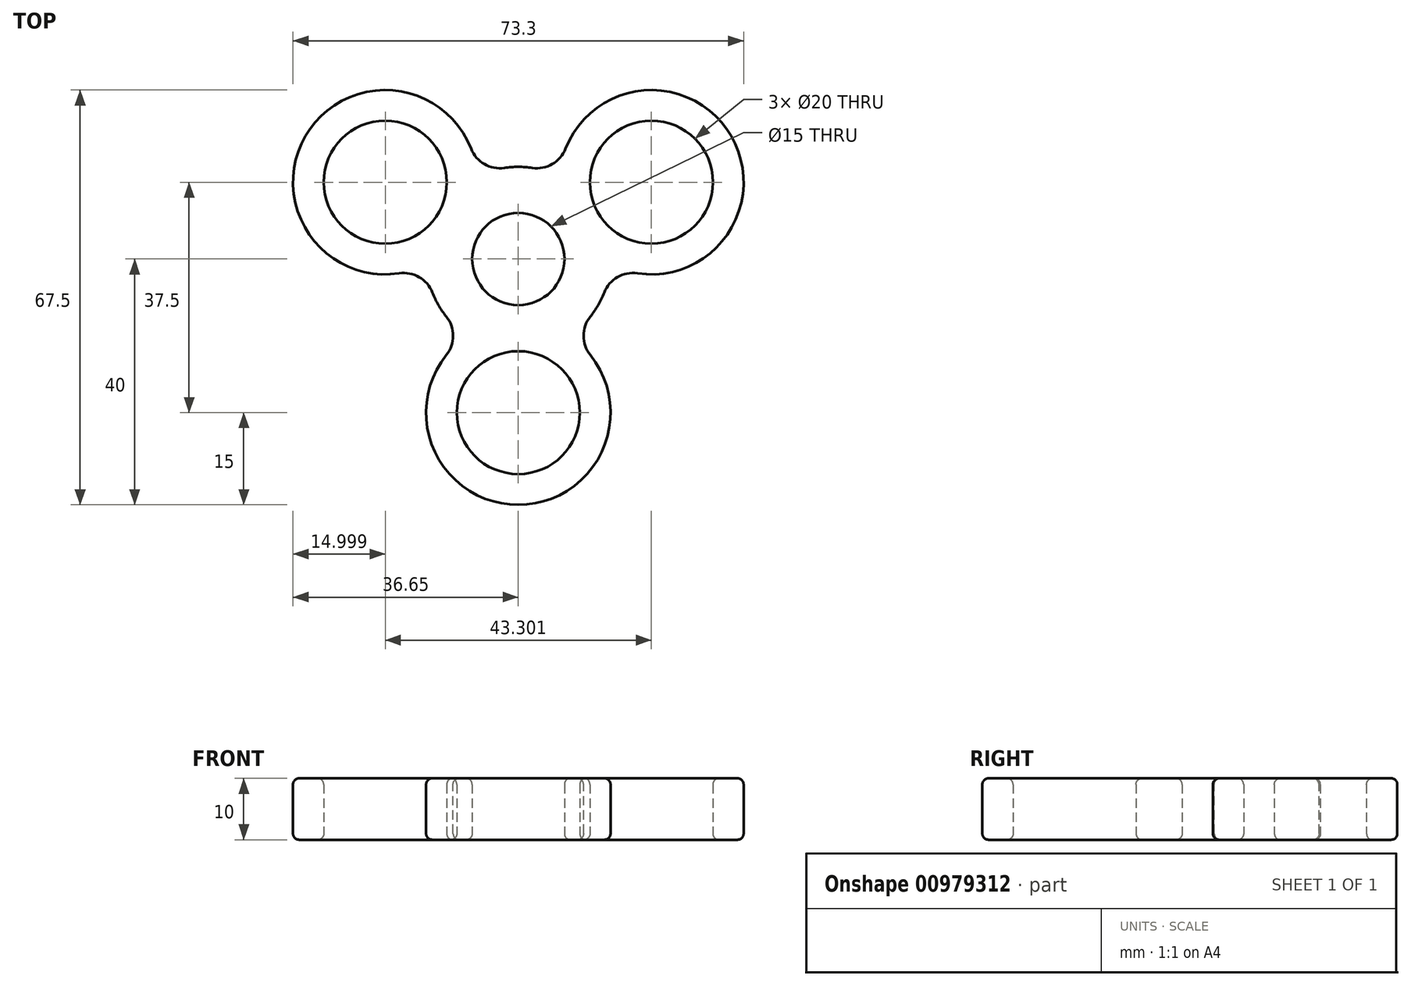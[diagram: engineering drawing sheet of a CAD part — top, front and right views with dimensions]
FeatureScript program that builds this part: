
annotation { "Feature Type Name" : "Feature", "Feature Type Description" : "" }
export const myFeature = defineFeature(function(context is Context, id is Id, definition is map)
    precondition{}
    {
        {
            var Q0;
            Q0=qCreatedBy(makeId("Top.planeOp"),FACE);
            var sketch = newSketch(context, id + "F0", { "sketchPlane" : qUnion([Q0])});
            skCircle(sketch, "E0", {"center": v(0, 0) * mm, "radius": 7.5 * mm});
            skCircle(sketch, "E1", {"center": v(0, 0) * mm, "radius": 15 * mm});
            skLineSegment(sketch, "E2", {"start": v(0, 0) * mm, "end": v(0, -25) * mm, "construction": true});
            skCircle(sketch, "E3", {"center": v(0, -25) * mm, "radius": 15 * mm});
            skCircle(sketch, "E4", {"center": v(0, -25) * mm, "radius": 10 * mm});
            skCircle(sketch, "E5.1.0", {"center": v(21.65, 12.5) * mm, "radius": 15 * mm});
            skCircle(sketch, "E5.1.1", {"center": v(21.65, 12.5) * mm, "radius": 10 * mm});
            skCircle(sketch, "E5.2.0", {"center": v(-21.65, 12.5) * mm, "radius": 15 * mm});
            skCircle(sketch, "E5.2.1", {"center": v(-21.65, 12.5) * mm, "radius": 10 * mm});
            skSolve(sketch);
        }
        {
            var Q0;
            {var subQ3=sQuery(id+"F0.wireOp",EDGE,"E5.2.1");Q0=makeQuery(id+"F0.imprint","IMPRINT",FACE,{"disambiguationData":[TD([[makeQuery(id+"F0.imprint","IMPRINT",EDGE,{"derivedFrom":subQ3}),-1.0]])]});}
            var Q1;
            {var subQ0=sQuery(id+"F0.wireOp",EDGE,"E5.2.0");var subQ1=sQuery(id+"F0.wireOp",EDGE,"E1");var subQ2=makeQuery(id+"F0.imprint","INTERSECT",VERTEX,{"disambiguationData":[OD(0.0)],"derivedFrom":[subQ1,subQ0]});Q1=makeQuery(id+"F0.imprint","IMPRINT",FACE,{"disambiguationData":[TD([[makeQuery(id+"F0.imprint","IMPRINT",EDGE,{"disambiguationData":[TD([[subQ2,-1.0]])],"derivedFrom":subQ1}),1.0]])]});}
            var Q2;
            Q2=makeQuery(id+"F0.imprint","IMPRINT",FACE,{"disambiguationData":[TD([[makeQuery(id+"F0.imprint","IMPRINT",EDGE,{"derivedFrom":sQuery(id+"F0.wireOp",EDGE,"E0")}),-1.0]])]});
            var Q3;
            {var subQ0=sQuery(id+"F0.wireOp",EDGE,"E5.1.0");var subQ1=sQuery(id+"F0.wireOp",EDGE,"E1");var subQ2=makeQuery(id+"F0.imprint","INTERSECT",VERTEX,{"disambiguationData":[OD(0.0)],"derivedFrom":[subQ1,subQ0]});Q3=makeQuery(id+"F0.imprint","IMPRINT",FACE,{"disambiguationData":[TD([[makeQuery(id+"F0.imprint","IMPRINT",EDGE,{"disambiguationData":[TD([[subQ2,1.0]])],"derivedFrom":subQ1}),1.0]])]});}
            var Q4;
            {var subQ3=sQuery(id+"F0.wireOp",EDGE,"E5.1.1");Q4=makeQuery(id+"F0.imprint","IMPRINT",FACE,{"disambiguationData":[TD([[makeQuery(id+"F0.imprint","IMPRINT",EDGE,{"derivedFrom":subQ3}),-1.0]])]});}
            var Q5;
            {var subQ0=sQuery(id+"F0.wireOp",EDGE,"E3");var subQ1=sQuery(id+"F0.wireOp",EDGE,"E1");var subQ2=makeQuery(id+"F0.imprint","INTERSECT",VERTEX,{"disambiguationData":[OD(0.0)],"derivedFrom":[subQ1,subQ0]});Q5=makeQuery(id+"F0.imprint","IMPRINT",FACE,{"disambiguationData":[TD([[makeQuery(id+"F0.imprint","IMPRINT",EDGE,{"disambiguationData":[TD([[subQ2,-1.0]])],"derivedFrom":subQ1}),1.0]])]});}
            var Q6;
            {var subQ3=sQuery(id+"F0.wireOp",EDGE,"E4");Q6=makeQuery(id+"F0.imprint","IMPRINT",FACE,{"disambiguationData":[TD([[makeQuery(id+"F0.imprint","IMPRINT",EDGE,{"derivedFrom":subQ3}),-1.0]])]});}
            extrude(context, id + "F1", {"entities" : qUnion([Q0, Q1, Q2, Q3, Q4, Q5, Q6]), "depth" : 10 * mm, "offsetDistance" : 25 * mm});
        }
        {
            var Q0;
            {var subQ0=sQuery(id+"F0.wireOp",EDGE,"E5.1.0");var subQ1=sQuery(id+"F0.wireOp",EDGE,"E1");Q0=makeQuery(id+"F1.opExtrude","SWEPT_EDGE",EDGE,{"disambiguationData":[OSD([subQ1,subQ0]),TDD([makeQuery(id+"F0.imprint","INTERSECT",VERTEX,{"disambiguationData":[OD(1.0)],"derivedFrom":[subQ1,subQ0]})])]});}
            var Q1;
            {var subQ0=sQuery(id+"F0.wireOp",EDGE,"E3");var subQ1=sQuery(id+"F0.wireOp",EDGE,"E1");Q1=makeQuery(id+"F1.opExtrude","SWEPT_EDGE",EDGE,{"disambiguationData":[OSD([subQ1,subQ0]),TDD([makeQuery(id+"F0.imprint","INTERSECT",VERTEX,{"disambiguationData":[OD(1.0)],"derivedFrom":[subQ1,subQ0]})])]});}
            var Q2;
            {var subQ0=sQuery(id+"F0.wireOp",EDGE,"E5.1.0");var subQ1=sQuery(id+"F0.wireOp",EDGE,"E1");Q2=makeQuery(id+"F1.opExtrude","SWEPT_EDGE",EDGE,{"disambiguationData":[OSD([subQ1,subQ0]),TDD([makeQuery(id+"F0.imprint","INTERSECT",VERTEX,{"disambiguationData":[OD(0.0)],"derivedFrom":[subQ1,subQ0]})])]});}
            var Q3;
            {var subQ0=sQuery(id+"F0.wireOp",EDGE,"E5.2.0");var subQ1=sQuery(id+"F0.wireOp",EDGE,"E1");Q3=makeQuery(id+"F1.opExtrude","SWEPT_EDGE",EDGE,{"disambiguationData":[OSD([subQ1,subQ0]),TDD([makeQuery(id+"F0.imprint","INTERSECT",VERTEX,{"disambiguationData":[OD(0.0)],"derivedFrom":[subQ1,subQ0]})])]});}
            var Q4;
            {var subQ0=sQuery(id+"F0.wireOp",EDGE,"E5.2.0");var subQ1=sQuery(id+"F0.wireOp",EDGE,"E1");Q4=makeQuery(id+"F1.opExtrude","SWEPT_EDGE",EDGE,{"disambiguationData":[OSD([subQ1,subQ0]),TDD([makeQuery(id+"F0.imprint","INTERSECT",VERTEX,{"disambiguationData":[OD(1.0)],"derivedFrom":[subQ1,subQ0]})])]});}
            var Q5;
            {var subQ0=sQuery(id+"F0.wireOp",EDGE,"E3");var subQ1=sQuery(id+"F0.wireOp",EDGE,"E1");Q5=makeQuery(id+"F1.opExtrude","SWEPT_EDGE",EDGE,{"disambiguationData":[OSD([subQ1,subQ0]),TDD([makeQuery(id+"F0.imprint","INTERSECT",VERTEX,{"disambiguationData":[OD(0.0)],"derivedFrom":[subQ1,subQ0]})])]});}
            fillet(context, id + "F2", {"entities" : qUnion([Q0, Q1, Q2, Q3, Q4, Q5]), "radius" : 5 * mm, "tangentPropagation" : true, "allowEdgeOverflow" : false});
        }
        {
            var Q0;
            {var subQ0=sQuery(id+"F0.wireOp",EDGE,"E5.2.0");var subQ1=sQuery(id+"F0.wireOp",EDGE,"E1");Q0=makeQuery(id+"F2.opFillet","BLEND_EDGE",EDGE,{"blendedFrom":[makeQuery(id+"F1.opExtrude","SWEPT_EDGE",EDGE,{"disambiguationData":[OSD([subQ1,subQ0]),TDD([makeQuery(id+"F0.imprint","INTERSECT",VERTEX,{"disambiguationData":[OD(1.0)],"derivedFrom":[subQ1,subQ0]})])]}),makeQuery(id+"F1.opExtrude","CAP_FACE",FACE,{"disambiguationData":[OSD([sQuery(id+"F0.wireOp",EDGE,"E0"),subQ1,sQuery(id+"F0.wireOp",EDGE,"E3"),sQuery(id+"F0.wireOp",EDGE,"E4"),sQuery(id+"F0.wireOp",EDGE,"E5.1.0"),sQuery(id+"F0.wireOp",EDGE,"E5.1.1"),subQ0,sQuery(id+"F0.wireOp",EDGE,"E5.2.1")])],"isStart":true})],"blendedInto":[makeQuery(id+"F1.opExtrude","CAP_FACE",FACE,{"disambiguationData":[OSD([sQuery(id+"F0.wireOp",EDGE,"E0"),subQ1,sQuery(id+"F0.wireOp",EDGE,"E3"),sQuery(id+"F0.wireOp",EDGE,"E4"),sQuery(id+"F0.wireOp",EDGE,"E5.1.0"),sQuery(id+"F0.wireOp",EDGE,"E5.1.1"),subQ0,sQuery(id+"F0.wireOp",EDGE,"E5.2.1")])],"isStart":true})]});}
            var Q1;
            {var subQ0=sQuery(id+"F0.wireOp",EDGE,"E5.2.0");var subQ1=sQuery(id+"F0.wireOp",EDGE,"E1");Q1=makeQuery(id+"F2.opFillet","BLEND_EDGE",EDGE,{"blendedFrom":[makeQuery(id+"F1.opExtrude","SWEPT_EDGE",EDGE,{"disambiguationData":[OSD([subQ1,subQ0]),TDD([makeQuery(id+"F0.imprint","INTERSECT",VERTEX,{"disambiguationData":[OD(0.0)],"derivedFrom":[subQ1,subQ0]})])]}),makeQuery(id+"F1.opExtrude","CAP_FACE",FACE,{"disambiguationData":[OSD([sQuery(id+"F0.wireOp",EDGE,"E0"),subQ1,sQuery(id+"F0.wireOp",EDGE,"E3"),sQuery(id+"F0.wireOp",EDGE,"E4"),sQuery(id+"F0.wireOp",EDGE,"E5.1.0"),sQuery(id+"F0.wireOp",EDGE,"E5.1.1"),subQ0,sQuery(id+"F0.wireOp",EDGE,"E5.2.1")])],"isStart":false})],"blendedInto":[makeQuery(id+"F1.opExtrude","CAP_FACE",FACE,{"disambiguationData":[OSD([sQuery(id+"F0.wireOp",EDGE,"E0"),subQ1,sQuery(id+"F0.wireOp",EDGE,"E3"),sQuery(id+"F0.wireOp",EDGE,"E4"),sQuery(id+"F0.wireOp",EDGE,"E5.1.0"),sQuery(id+"F0.wireOp",EDGE,"E5.1.1"),subQ0,sQuery(id+"F0.wireOp",EDGE,"E5.2.1")])],"isStart":false})]});}
            var Q2;
            Q2=makeQuery(id+"F1.opExtrude","CAP_EDGE",EDGE,{"disambiguationData":[OSD([sQuery(id+"F0.wireOp",EDGE,"E0")])],"isStart":true});
            var Q3;
            Q3=makeQuery(id+"F1.opExtrude","CAP_EDGE",EDGE,{"disambiguationData":[OSD([sQuery(id+"F0.wireOp",EDGE,"E0")])],"isStart":false});
            var Q4;
            {var subQ0=sQuery(id+"F0.wireOp",EDGE,"E5.1.0");var subQ1=sQuery(id+"F0.wireOp",EDGE,"E1");Q4=makeQuery(id+"F2.opFillet","BLEND_EDGE",EDGE,{"blendedFrom":[makeQuery(id+"F1.opExtrude","SWEPT_EDGE",EDGE,{"disambiguationData":[OSD([subQ1,subQ0]),TDD([makeQuery(id+"F0.imprint","INTERSECT",VERTEX,{"disambiguationData":[OD(0.0)],"derivedFrom":[subQ1,subQ0]})])]}),makeQuery(id+"F1.opExtrude","CAP_FACE",FACE,{"disambiguationData":[OSD([sQuery(id+"F0.wireOp",EDGE,"E0"),subQ1,sQuery(id+"F0.wireOp",EDGE,"E3"),sQuery(id+"F0.wireOp",EDGE,"E4"),subQ0,sQuery(id+"F0.wireOp",EDGE,"E5.1.1"),sQuery(id+"F0.wireOp",EDGE,"E5.2.0"),sQuery(id+"F0.wireOp",EDGE,"E5.2.1")])],"isStart":false})],"blendedInto":[makeQuery(id+"F1.opExtrude","CAP_FACE",FACE,{"disambiguationData":[OSD([sQuery(id+"F0.wireOp",EDGE,"E0"),subQ1,sQuery(id+"F0.wireOp",EDGE,"E3"),sQuery(id+"F0.wireOp",EDGE,"E4"),subQ0,sQuery(id+"F0.wireOp",EDGE,"E5.1.1"),sQuery(id+"F0.wireOp",EDGE,"E5.2.0"),sQuery(id+"F0.wireOp",EDGE,"E5.2.1")])],"isStart":false})]});}
            var Q5;
            {var subQ0=sQuery(id+"F0.wireOp",EDGE,"E3");var subQ1=sQuery(id+"F0.wireOp",EDGE,"E1");Q5=makeQuery(id+"F2.opFillet","BLEND_EDGE",EDGE,{"blendedFrom":[makeQuery(id+"F1.opExtrude","SWEPT_EDGE",EDGE,{"disambiguationData":[OSD([subQ1,subQ0]),TDD([makeQuery(id+"F0.imprint","INTERSECT",VERTEX,{"disambiguationData":[OD(0.0)],"derivedFrom":[subQ1,subQ0]})])]}),makeQuery(id+"F1.opExtrude","CAP_FACE",FACE,{"disambiguationData":[OSD([sQuery(id+"F0.wireOp",EDGE,"E0"),subQ1,subQ0,sQuery(id+"F0.wireOp",EDGE,"E4"),sQuery(id+"F0.wireOp",EDGE,"E5.1.0"),sQuery(id+"F0.wireOp",EDGE,"E5.1.1"),sQuery(id+"F0.wireOp",EDGE,"E5.2.0"),sQuery(id+"F0.wireOp",EDGE,"E5.2.1")])],"isStart":false})],"blendedInto":[makeQuery(id+"F1.opExtrude","CAP_FACE",FACE,{"disambiguationData":[OSD([sQuery(id+"F0.wireOp",EDGE,"E0"),subQ1,subQ0,sQuery(id+"F0.wireOp",EDGE,"E4"),sQuery(id+"F0.wireOp",EDGE,"E5.1.0"),sQuery(id+"F0.wireOp",EDGE,"E5.1.1"),sQuery(id+"F0.wireOp",EDGE,"E5.2.0"),sQuery(id+"F0.wireOp",EDGE,"E5.2.1")])],"isStart":false})]});}
            var Q6;
            Q6=makeQuery(id+"F1.opExtrude","CAP_EDGE",EDGE,{"disambiguationData":[OSD([sQuery(id+"F0.wireOp",EDGE,"E4")])],"isStart":true});
            var Q7;
            Q7=makeQuery(id+"F1.opExtrude","CAP_EDGE",EDGE,{"disambiguationData":[OSD([sQuery(id+"F0.wireOp",EDGE,"E4")])],"isStart":false});
            var Q8;
            Q8=makeQuery(id+"F1.opExtrude","CAP_EDGE",EDGE,{"disambiguationData":[OSD([sQuery(id+"F0.wireOp",EDGE,"E5.1.1")])],"isStart":true});
            var Q9;
            Q9=makeQuery(id+"F1.opExtrude","CAP_EDGE",EDGE,{"disambiguationData":[OSD([sQuery(id+"F0.wireOp",EDGE,"E5.1.1")])],"isStart":false});
            var Q10;
            {var subQ0=sQuery(id+"F0.wireOp",EDGE,"E5.2.0");var subQ1=sQuery(id+"F0.wireOp",EDGE,"E1");Q10=makeQuery(id+"F2.opFillet","BLEND_EDGE",EDGE,{"blendedFrom":[makeQuery(id+"F1.opExtrude","SWEPT_EDGE",EDGE,{"disambiguationData":[OSD([subQ1,subQ0]),TDD([makeQuery(id+"F0.imprint","INTERSECT",VERTEX,{"disambiguationData":[OD(1.0)],"derivedFrom":[subQ1,subQ0]})])]}),makeQuery(id+"F1.opExtrude","CAP_FACE",FACE,{"disambiguationData":[OSD([sQuery(id+"F0.wireOp",EDGE,"E0"),subQ1,sQuery(id+"F0.wireOp",EDGE,"E3"),sQuery(id+"F0.wireOp",EDGE,"E4"),sQuery(id+"F0.wireOp",EDGE,"E5.1.0"),sQuery(id+"F0.wireOp",EDGE,"E5.1.1"),subQ0,sQuery(id+"F0.wireOp",EDGE,"E5.2.1")])],"isStart":false})],"blendedInto":[makeQuery(id+"F1.opExtrude","CAP_FACE",FACE,{"disambiguationData":[OSD([sQuery(id+"F0.wireOp",EDGE,"E0"),subQ1,sQuery(id+"F0.wireOp",EDGE,"E3"),sQuery(id+"F0.wireOp",EDGE,"E4"),sQuery(id+"F0.wireOp",EDGE,"E5.1.0"),sQuery(id+"F0.wireOp",EDGE,"E5.1.1"),subQ0,sQuery(id+"F0.wireOp",EDGE,"E5.2.1")])],"isStart":false})]});}
            var Q11;
            Q11=makeQuery(id+"F1.opExtrude","CAP_EDGE",EDGE,{"disambiguationData":[OSD([sQuery(id+"F0.wireOp",EDGE,"E5.2.1")])],"isStart":true});
            var Q12;
            Q12=makeQuery(id+"F1.opExtrude","CAP_EDGE",EDGE,{"disambiguationData":[OSD([sQuery(id+"F0.wireOp",EDGE,"E5.2.1")])],"isStart":false});
            var Q13;
            {var subQ0=sQuery(id+"F0.wireOp",EDGE,"E1");Q13=makeQuery(id+"F1.opExtrude","CAP_EDGE",EDGE,{"disambiguationData":[OSD([subQ0]),TDD([makeQuery(id+"F0.imprint","IMPRINT",EDGE,{"disambiguationData":[TD([[makeQuery(id+"F0.imprint","INTERSECT",VERTEX,{"disambiguationData":[OD(1.0)],"derivedFrom":[subQ0,sQuery(id+"F0.wireOp",EDGE,"E3")]}),-1.0]])],"derivedFrom":subQ0})])],"isStart":false});}
            var Q14;
            Q14=makeQuery(id+"F1.opExtrude","CAP_EDGE",EDGE,{"disambiguationData":[OSD([sQuery(id+"F0.wireOp",EDGE,"E3")])],"isStart":true});
            var Q15;
            Q15=makeQuery(id+"F1.opExtrude","CAP_EDGE",EDGE,{"disambiguationData":[OSD([sQuery(id+"F0.wireOp",EDGE,"E3")])],"isStart":false});
            var Q16;
            Q16=makeQuery(id+"F1.opExtrude","CAP_EDGE",EDGE,{"disambiguationData":[OSD([sQuery(id+"F0.wireOp",EDGE,"E5.1.0")])],"isStart":true});
            var Q17;
            {var subQ0=sQuery(id+"F0.wireOp",EDGE,"E3");var subQ1=sQuery(id+"F0.wireOp",EDGE,"E1");Q17=makeQuery(id+"F2.opFillet","BLEND_EDGE",EDGE,{"blendedFrom":[makeQuery(id+"F1.opExtrude","SWEPT_EDGE",EDGE,{"disambiguationData":[OSD([subQ1,subQ0]),TDD([makeQuery(id+"F0.imprint","INTERSECT",VERTEX,{"disambiguationData":[OD(1.0)],"derivedFrom":[subQ1,subQ0]})])]}),makeQuery(id+"F1.opExtrude","CAP_FACE",FACE,{"disambiguationData":[OSD([sQuery(id+"F0.wireOp",EDGE,"E0"),subQ1,subQ0,sQuery(id+"F0.wireOp",EDGE,"E4"),sQuery(id+"F0.wireOp",EDGE,"E5.1.0"),sQuery(id+"F0.wireOp",EDGE,"E5.1.1"),sQuery(id+"F0.wireOp",EDGE,"E5.2.0"),sQuery(id+"F0.wireOp",EDGE,"E5.2.1")])],"isStart":false})],"blendedInto":[makeQuery(id+"F1.opExtrude","CAP_FACE",FACE,{"disambiguationData":[OSD([sQuery(id+"F0.wireOp",EDGE,"E0"),subQ1,subQ0,sQuery(id+"F0.wireOp",EDGE,"E4"),sQuery(id+"F0.wireOp",EDGE,"E5.1.0"),sQuery(id+"F0.wireOp",EDGE,"E5.1.1"),sQuery(id+"F0.wireOp",EDGE,"E5.2.0"),sQuery(id+"F0.wireOp",EDGE,"E5.2.1")])],"isStart":false})]});}
            var Q18;
            Q18=makeQuery(id+"F1.opExtrude","CAP_EDGE",EDGE,{"disambiguationData":[OSD([sQuery(id+"F0.wireOp",EDGE,"E5.1.0")])],"isStart":false});
            var Q19;
            Q19=makeQuery(id+"F1.opExtrude","CAP_EDGE",EDGE,{"disambiguationData":[OSD([sQuery(id+"F0.wireOp",EDGE,"E5.2.0")])],"isStart":true});
            var Q20;
            Q20=makeQuery(id+"F1.opExtrude","CAP_EDGE",EDGE,{"disambiguationData":[OSD([sQuery(id+"F0.wireOp",EDGE,"E5.2.0")])],"isStart":false});
            var Q21;
            {var subQ0=sQuery(id+"F0.wireOp",EDGE,"E5.1.0");var subQ1=sQuery(id+"F0.wireOp",EDGE,"E1");Q21=makeQuery(id+"F2.opFillet","BLEND_EDGE",EDGE,{"blendedFrom":[makeQuery(id+"F1.opExtrude","SWEPT_EDGE",EDGE,{"disambiguationData":[OSD([subQ1,subQ0]),TDD([makeQuery(id+"F0.imprint","INTERSECT",VERTEX,{"disambiguationData":[OD(1.0)],"derivedFrom":[subQ1,subQ0]})])]}),makeQuery(id+"F1.opExtrude","CAP_FACE",FACE,{"disambiguationData":[OSD([sQuery(id+"F0.wireOp",EDGE,"E0"),subQ1,sQuery(id+"F0.wireOp",EDGE,"E3"),sQuery(id+"F0.wireOp",EDGE,"E4"),subQ0,sQuery(id+"F0.wireOp",EDGE,"E5.1.1"),sQuery(id+"F0.wireOp",EDGE,"E5.2.0"),sQuery(id+"F0.wireOp",EDGE,"E5.2.1")])],"isStart":false})],"blendedInto":[makeQuery(id+"F1.opExtrude","CAP_FACE",FACE,{"disambiguationData":[OSD([sQuery(id+"F0.wireOp",EDGE,"E0"),subQ1,sQuery(id+"F0.wireOp",EDGE,"E3"),sQuery(id+"F0.wireOp",EDGE,"E4"),subQ0,sQuery(id+"F0.wireOp",EDGE,"E5.1.1"),sQuery(id+"F0.wireOp",EDGE,"E5.2.0"),sQuery(id+"F0.wireOp",EDGE,"E5.2.1")])],"isStart":false})]});}
            var Q22;
            {var subQ0=sQuery(id+"F0.wireOp",EDGE,"E5.1.0");var subQ1=sQuery(id+"F0.wireOp",EDGE,"E1");Q22=makeQuery(id+"F2.opFillet","BLEND_EDGE",EDGE,{"blendedFrom":[makeQuery(id+"F1.opExtrude","SWEPT_EDGE",EDGE,{"disambiguationData":[OSD([subQ1,subQ0]),TDD([makeQuery(id+"F0.imprint","INTERSECT",VERTEX,{"disambiguationData":[OD(1.0)],"derivedFrom":[subQ1,subQ0]})])]}),makeQuery(id+"F1.opExtrude","SWEPT_FACE",FACE,{"disambiguationData":[OSD([subQ0])]})],"blendedInto":[makeQuery(id+"F1.opExtrude","SWEPT_FACE",FACE,{"disambiguationData":[OSD([subQ0])]})]});}
            var Q23;
            {var subQ0=sQuery(id+"F0.wireOp",EDGE,"E1");Q23=makeQuery(id+"F1.opExtrude","CAP_EDGE",EDGE,{"disambiguationData":[OSD([subQ0]),TDD([makeQuery(id+"F0.imprint","IMPRINT",EDGE,{"disambiguationData":[TD([[makeQuery(id+"F0.imprint","INTERSECT",VERTEX,{"disambiguationData":[OD(1.0)],"derivedFrom":[subQ0,sQuery(id+"F0.wireOp",EDGE,"E5.2.0")]}),-1.0]])],"derivedFrom":subQ0})])],"isStart":false});}
            var Q24;
            {var subQ0=sQuery(id+"F0.wireOp",EDGE,"E1");Q24=makeQuery(id+"F1.opExtrude","CAP_EDGE",EDGE,{"disambiguationData":[OSD([subQ0]),TDD([makeQuery(id+"F0.imprint","IMPRINT",EDGE,{"disambiguationData":[TD([[makeQuery(id+"F0.imprint","INTERSECT",VERTEX,{"disambiguationData":[OD(1.0)],"derivedFrom":[subQ0,sQuery(id+"F0.wireOp",EDGE,"E3")]}),-1.0]])],"derivedFrom":subQ0})])],"isStart":true});}
            var Q25;
            {var subQ0=sQuery(id+"F0.wireOp",EDGE,"E5.2.0");var subQ1=sQuery(id+"F0.wireOp",EDGE,"E1");Q25=makeQuery(id+"F2.opFillet","BLEND_EDGE",EDGE,{"blendedFrom":[makeQuery(id+"F1.opExtrude","SWEPT_EDGE",EDGE,{"disambiguationData":[OSD([subQ1,subQ0]),TDD([makeQuery(id+"F0.imprint","INTERSECT",VERTEX,{"disambiguationData":[OD(0.0)],"derivedFrom":[subQ1,subQ0]})])]}),makeQuery(id+"F1.opExtrude","SWEPT_FACE",FACE,{"disambiguationData":[OSD([subQ0])]})],"blendedInto":[makeQuery(id+"F1.opExtrude","SWEPT_FACE",FACE,{"disambiguationData":[OSD([subQ0])]})]});}
            var Q26;
            {var subQ0=sQuery(id+"F0.wireOp",EDGE,"E1");var subQ1=sQuery(id+"F0.wireOp",EDGE,"E5.2.0");var subQ2=makeQuery(id+"F0.imprint","INTERSECT",VERTEX,{"disambiguationData":[OD(0.0)],"derivedFrom":[subQ0,subQ1]});Q26=makeQuery(id+"F2.opFillet","BLEND_EDGE",EDGE,{"blendedFrom":[makeQuery(id+"F1.opExtrude","SWEPT_EDGE",EDGE,{"disambiguationData":[OSD([subQ0,subQ1]),TDD([subQ2])]}),makeQuery(id+"F1.opExtrude","SWEPT_FACE",FACE,{"disambiguationData":[OSD([subQ0]),TDD([makeQuery(id+"F0.imprint","IMPRINT",EDGE,{"disambiguationData":[TD([[makeQuery(id+"F0.imprint","INTERSECT",VERTEX,{"disambiguationData":[OD(0.0)],"derivedFrom":[subQ0,sQuery(id+"F0.wireOp",EDGE,"E5.1.0")]}),-1.0]])],"derivedFrom":subQ0})])]})],"blendedInto":[makeQuery(id+"F1.opExtrude","SWEPT_FACE",FACE,{"disambiguationData":[OSD([subQ0]),TDD([makeQuery(id+"F0.imprint","IMPRINT",EDGE,{"disambiguationData":[TD([[makeQuery(id+"F0.imprint","INTERSECT",VERTEX,{"disambiguationData":[OD(0.0)],"derivedFrom":[subQ0,sQuery(id+"F0.wireOp",EDGE,"E5.1.0")]}),-1.0]])],"derivedFrom":subQ0})])]})]});}
            var Q27;
            {var subQ0=sQuery(id+"F0.wireOp",EDGE,"E5.2.0");var subQ1=sQuery(id+"F0.wireOp",EDGE,"E1");Q27=makeQuery(id+"F2.opFillet","BLEND_EDGE",EDGE,{"blendedFrom":[makeQuery(id+"F1.opExtrude","SWEPT_EDGE",EDGE,{"disambiguationData":[OSD([subQ1,subQ0]),TDD([makeQuery(id+"F0.imprint","INTERSECT",VERTEX,{"disambiguationData":[OD(0.0)],"derivedFrom":[subQ1,subQ0]})])]}),makeQuery(id+"F1.opExtrude","CAP_FACE",FACE,{"disambiguationData":[OSD([sQuery(id+"F0.wireOp",EDGE,"E0"),subQ1,sQuery(id+"F0.wireOp",EDGE,"E3"),sQuery(id+"F0.wireOp",EDGE,"E4"),sQuery(id+"F0.wireOp",EDGE,"E5.1.0"),sQuery(id+"F0.wireOp",EDGE,"E5.1.1"),subQ0,sQuery(id+"F0.wireOp",EDGE,"E5.2.1")])],"isStart":true})],"blendedInto":[makeQuery(id+"F1.opExtrude","CAP_FACE",FACE,{"disambiguationData":[OSD([sQuery(id+"F0.wireOp",EDGE,"E0"),subQ1,sQuery(id+"F0.wireOp",EDGE,"E3"),sQuery(id+"F0.wireOp",EDGE,"E4"),sQuery(id+"F0.wireOp",EDGE,"E5.1.0"),sQuery(id+"F0.wireOp",EDGE,"E5.1.1"),subQ0,sQuery(id+"F0.wireOp",EDGE,"E5.2.1")])],"isStart":true})]});}
            var Q28;
            {var subQ0=sQuery(id+"F0.wireOp",EDGE,"E5.1.0");var subQ1=sQuery(id+"F0.wireOp",EDGE,"E1");Q28=makeQuery(id+"F2.opFillet","BLEND_EDGE",EDGE,{"blendedFrom":[makeQuery(id+"F1.opExtrude","SWEPT_EDGE",EDGE,{"disambiguationData":[OSD([subQ1,subQ0]),TDD([makeQuery(id+"F0.imprint","INTERSECT",VERTEX,{"disambiguationData":[OD(0.0)],"derivedFrom":[subQ1,subQ0]})])]}),makeQuery(id+"F1.opExtrude","SWEPT_FACE",FACE,{"disambiguationData":[OSD([subQ0])]})],"blendedInto":[makeQuery(id+"F1.opExtrude","SWEPT_FACE",FACE,{"disambiguationData":[OSD([subQ0])]})]});}
            var Q29;
            {var subQ0=sQuery(id+"F0.wireOp",EDGE,"E5.1.0");var subQ1=sQuery(id+"F0.wireOp",EDGE,"E1");var subQ2=makeQuery(id+"F0.imprint","INTERSECT",VERTEX,{"disambiguationData":[OD(0.0)],"derivedFrom":[subQ1,subQ0]});Q29=makeQuery(id+"F2.opFillet","BLEND_EDGE",EDGE,{"blendedFrom":[makeQuery(id+"F1.opExtrude","SWEPT_EDGE",EDGE,{"disambiguationData":[OSD([subQ1,subQ0]),TDD([subQ2])]}),makeQuery(id+"F1.opExtrude","SWEPT_FACE",FACE,{"disambiguationData":[OSD([subQ1]),TDD([makeQuery(id+"F0.imprint","IMPRINT",EDGE,{"disambiguationData":[TD([[subQ2,-1.0]])],"derivedFrom":subQ1})])]})],"blendedInto":[makeQuery(id+"F1.opExtrude","SWEPT_FACE",FACE,{"disambiguationData":[OSD([subQ1]),TDD([makeQuery(id+"F0.imprint","IMPRINT",EDGE,{"disambiguationData":[TD([[subQ2,-1.0]])],"derivedFrom":subQ1})])]})]});}
            var Q30;
            {var subQ0=sQuery(id+"F0.wireOp",EDGE,"E5.1.0");var subQ1=sQuery(id+"F0.wireOp",EDGE,"E1");Q30=makeQuery(id+"F2.opFillet","BLEND_EDGE",EDGE,{"blendedFrom":[makeQuery(id+"F1.opExtrude","SWEPT_EDGE",EDGE,{"disambiguationData":[OSD([subQ1,subQ0]),TDD([makeQuery(id+"F0.imprint","INTERSECT",VERTEX,{"disambiguationData":[OD(0.0)],"derivedFrom":[subQ1,subQ0]})])]}),makeQuery(id+"F1.opExtrude","CAP_FACE",FACE,{"disambiguationData":[OSD([sQuery(id+"F0.wireOp",EDGE,"E0"),subQ1,sQuery(id+"F0.wireOp",EDGE,"E3"),sQuery(id+"F0.wireOp",EDGE,"E4"),subQ0,sQuery(id+"F0.wireOp",EDGE,"E5.1.1"),sQuery(id+"F0.wireOp",EDGE,"E5.2.0"),sQuery(id+"F0.wireOp",EDGE,"E5.2.1")])],"isStart":true})],"blendedInto":[makeQuery(id+"F1.opExtrude","CAP_FACE",FACE,{"disambiguationData":[OSD([sQuery(id+"F0.wireOp",EDGE,"E0"),subQ1,sQuery(id+"F0.wireOp",EDGE,"E3"),sQuery(id+"F0.wireOp",EDGE,"E4"),subQ0,sQuery(id+"F0.wireOp",EDGE,"E5.1.1"),sQuery(id+"F0.wireOp",EDGE,"E5.2.0"),sQuery(id+"F0.wireOp",EDGE,"E5.2.1")])],"isStart":true})]});}
            var Q31;
            {var subQ0=sQuery(id+"F0.wireOp",EDGE,"E3");var subQ1=sQuery(id+"F0.wireOp",EDGE,"E1");Q31=makeQuery(id+"F2.opFillet","BLEND_EDGE",EDGE,{"blendedFrom":[makeQuery(id+"F1.opExtrude","SWEPT_EDGE",EDGE,{"disambiguationData":[OSD([subQ1,subQ0]),TDD([makeQuery(id+"F0.imprint","INTERSECT",VERTEX,{"disambiguationData":[OD(0.0)],"derivedFrom":[subQ1,subQ0]})])]}),makeQuery(id+"F1.opExtrude","SWEPT_FACE",FACE,{"disambiguationData":[OSD([subQ0])]})],"blendedInto":[makeQuery(id+"F1.opExtrude","SWEPT_FACE",FACE,{"disambiguationData":[OSD([subQ0])]})]});}
            var Q32;
            {var subQ0=sQuery(id+"F0.wireOp",EDGE,"E1");var subQ1=sQuery(id+"F0.wireOp",EDGE,"E3");var subQ2=makeQuery(id+"F0.imprint","INTERSECT",VERTEX,{"disambiguationData":[OD(0.0)],"derivedFrom":[subQ0,subQ1]});Q32=makeQuery(id+"F2.opFillet","BLEND_EDGE",EDGE,{"blendedFrom":[makeQuery(id+"F1.opExtrude","SWEPT_EDGE",EDGE,{"disambiguationData":[OSD([subQ0,subQ1]),TDD([subQ2])]}),makeQuery(id+"F1.opExtrude","SWEPT_FACE",FACE,{"disambiguationData":[OSD([subQ0]),TDD([makeQuery(id+"F0.imprint","IMPRINT",EDGE,{"disambiguationData":[TD([[makeQuery(id+"F0.imprint","INTERSECT",VERTEX,{"disambiguationData":[OD(1.0)],"derivedFrom":[subQ0,sQuery(id+"F0.wireOp",EDGE,"E5.2.0")]}),-1.0]])],"derivedFrom":subQ0})])]})],"blendedInto":[makeQuery(id+"F1.opExtrude","SWEPT_FACE",FACE,{"disambiguationData":[OSD([subQ0]),TDD([makeQuery(id+"F0.imprint","IMPRINT",EDGE,{"disambiguationData":[TD([[makeQuery(id+"F0.imprint","INTERSECT",VERTEX,{"disambiguationData":[OD(1.0)],"derivedFrom":[subQ0,sQuery(id+"F0.wireOp",EDGE,"E5.2.0")]}),-1.0]])],"derivedFrom":subQ0})])]})]});}
            var Q33;
            {var subQ0=sQuery(id+"F0.wireOp",EDGE,"E5.2.0");var subQ1=sQuery(id+"F0.wireOp",EDGE,"E1");var subQ2=makeQuery(id+"F0.imprint","INTERSECT",VERTEX,{"disambiguationData":[OD(1.0)],"derivedFrom":[subQ1,subQ0]});Q33=makeQuery(id+"F2.opFillet","BLEND_EDGE",EDGE,{"blendedFrom":[makeQuery(id+"F1.opExtrude","SWEPT_EDGE",EDGE,{"disambiguationData":[OSD([subQ1,subQ0]),TDD([subQ2])]}),makeQuery(id+"F1.opExtrude","SWEPT_FACE",FACE,{"disambiguationData":[OSD([subQ1]),TDD([makeQuery(id+"F0.imprint","IMPRINT",EDGE,{"disambiguationData":[TD([[subQ2,-1.0]])],"derivedFrom":subQ1})])]})],"blendedInto":[makeQuery(id+"F1.opExtrude","SWEPT_FACE",FACE,{"disambiguationData":[OSD([subQ1]),TDD([makeQuery(id+"F0.imprint","IMPRINT",EDGE,{"disambiguationData":[TD([[subQ2,-1.0]])],"derivedFrom":subQ1})])]})]});}
            var Q34;
            {var subQ0=sQuery(id+"F0.wireOp",EDGE,"E5.2.0");var subQ1=sQuery(id+"F0.wireOp",EDGE,"E1");Q34=makeQuery(id+"F2.opFillet","BLEND_EDGE",EDGE,{"blendedFrom":[makeQuery(id+"F1.opExtrude","SWEPT_EDGE",EDGE,{"disambiguationData":[OSD([subQ1,subQ0]),TDD([makeQuery(id+"F0.imprint","INTERSECT",VERTEX,{"disambiguationData":[OD(1.0)],"derivedFrom":[subQ1,subQ0]})])]}),makeQuery(id+"F1.opExtrude","SWEPT_FACE",FACE,{"disambiguationData":[OSD([subQ0])]})],"blendedInto":[makeQuery(id+"F1.opExtrude","SWEPT_FACE",FACE,{"disambiguationData":[OSD([subQ0])]})]});}
            var Q35;
            {var subQ0=sQuery(id+"F0.wireOp",EDGE,"E3");var subQ1=sQuery(id+"F0.wireOp",EDGE,"E1");Q35=makeQuery(id+"F2.opFillet","BLEND_EDGE",EDGE,{"blendedFrom":[makeQuery(id+"F1.opExtrude","SWEPT_EDGE",EDGE,{"disambiguationData":[OSD([subQ1,subQ0]),TDD([makeQuery(id+"F0.imprint","INTERSECT",VERTEX,{"disambiguationData":[OD(0.0)],"derivedFrom":[subQ1,subQ0]})])]}),makeQuery(id+"F1.opExtrude","CAP_FACE",FACE,{"disambiguationData":[OSD([sQuery(id+"F0.wireOp",EDGE,"E0"),subQ1,subQ0,sQuery(id+"F0.wireOp",EDGE,"E4"),sQuery(id+"F0.wireOp",EDGE,"E5.1.0"),sQuery(id+"F0.wireOp",EDGE,"E5.1.1"),sQuery(id+"F0.wireOp",EDGE,"E5.2.0"),sQuery(id+"F0.wireOp",EDGE,"E5.2.1")])],"isStart":true})],"blendedInto":[makeQuery(id+"F1.opExtrude","CAP_FACE",FACE,{"disambiguationData":[OSD([sQuery(id+"F0.wireOp",EDGE,"E0"),subQ1,subQ0,sQuery(id+"F0.wireOp",EDGE,"E4"),sQuery(id+"F0.wireOp",EDGE,"E5.1.0"),sQuery(id+"F0.wireOp",EDGE,"E5.1.1"),sQuery(id+"F0.wireOp",EDGE,"E5.2.0"),sQuery(id+"F0.wireOp",EDGE,"E5.2.1")])],"isStart":true})]});}
            var Q36;
            {var subQ0=sQuery(id+"F0.wireOp",EDGE,"E3");var subQ1=sQuery(id+"F0.wireOp",EDGE,"E1");Q36=makeQuery(id+"F2.opFillet","BLEND_EDGE",EDGE,{"blendedFrom":[makeQuery(id+"F1.opExtrude","SWEPT_EDGE",EDGE,{"disambiguationData":[OSD([subQ1,subQ0]),TDD([makeQuery(id+"F0.imprint","INTERSECT",VERTEX,{"disambiguationData":[OD(1.0)],"derivedFrom":[subQ1,subQ0]})])]}),makeQuery(id+"F1.opExtrude","CAP_FACE",FACE,{"disambiguationData":[OSD([sQuery(id+"F0.wireOp",EDGE,"E0"),subQ1,subQ0,sQuery(id+"F0.wireOp",EDGE,"E4"),sQuery(id+"F0.wireOp",EDGE,"E5.1.0"),sQuery(id+"F0.wireOp",EDGE,"E5.1.1"),sQuery(id+"F0.wireOp",EDGE,"E5.2.0"),sQuery(id+"F0.wireOp",EDGE,"E5.2.1")])],"isStart":true})],"blendedInto":[makeQuery(id+"F1.opExtrude","CAP_FACE",FACE,{"disambiguationData":[OSD([sQuery(id+"F0.wireOp",EDGE,"E0"),subQ1,subQ0,sQuery(id+"F0.wireOp",EDGE,"E4"),sQuery(id+"F0.wireOp",EDGE,"E5.1.0"),sQuery(id+"F0.wireOp",EDGE,"E5.1.1"),sQuery(id+"F0.wireOp",EDGE,"E5.2.0"),sQuery(id+"F0.wireOp",EDGE,"E5.2.1")])],"isStart":true})]});}
            var Q37;
            {var subQ0=sQuery(id+"F0.wireOp",EDGE,"E3");var subQ1=sQuery(id+"F0.wireOp",EDGE,"E1");var subQ2=makeQuery(id+"F0.imprint","INTERSECT",VERTEX,{"disambiguationData":[OD(1.0)],"derivedFrom":[subQ1,subQ0]});Q37=makeQuery(id+"F2.opFillet","BLEND_EDGE",EDGE,{"blendedFrom":[makeQuery(id+"F1.opExtrude","SWEPT_EDGE",EDGE,{"disambiguationData":[OSD([subQ1,subQ0]),TDD([subQ2])]}),makeQuery(id+"F1.opExtrude","SWEPT_FACE",FACE,{"disambiguationData":[OSD([subQ1]),TDD([makeQuery(id+"F0.imprint","IMPRINT",EDGE,{"disambiguationData":[TD([[subQ2,-1.0]])],"derivedFrom":subQ1})])]})],"blendedInto":[makeQuery(id+"F1.opExtrude","SWEPT_FACE",FACE,{"disambiguationData":[OSD([subQ1]),TDD([makeQuery(id+"F0.imprint","IMPRINT",EDGE,{"disambiguationData":[TD([[subQ2,-1.0]])],"derivedFrom":subQ1})])]})]});}
            var Q38;
            {var subQ0=sQuery(id+"F0.wireOp",EDGE,"E3");var subQ1=sQuery(id+"F0.wireOp",EDGE,"E1");Q38=makeQuery(id+"F2.opFillet","BLEND_EDGE",EDGE,{"blendedFrom":[makeQuery(id+"F1.opExtrude","SWEPT_EDGE",EDGE,{"disambiguationData":[OSD([subQ1,subQ0]),TDD([makeQuery(id+"F0.imprint","INTERSECT",VERTEX,{"disambiguationData":[OD(1.0)],"derivedFrom":[subQ1,subQ0]})])]}),makeQuery(id+"F1.opExtrude","SWEPT_FACE",FACE,{"disambiguationData":[OSD([subQ0])]})],"blendedInto":[makeQuery(id+"F1.opExtrude","SWEPT_FACE",FACE,{"disambiguationData":[OSD([subQ0])]})]});}
            var Q39;
            {var subQ0=sQuery(id+"F0.wireOp",EDGE,"E5.1.0");var subQ1=sQuery(id+"F0.wireOp",EDGE,"E1");Q39=makeQuery(id+"F2.opFillet","BLEND_EDGE",EDGE,{"blendedFrom":[makeQuery(id+"F1.opExtrude","SWEPT_EDGE",EDGE,{"disambiguationData":[OSD([subQ1,subQ0]),TDD([makeQuery(id+"F0.imprint","INTERSECT",VERTEX,{"disambiguationData":[OD(1.0)],"derivedFrom":[subQ1,subQ0]})])]}),makeQuery(id+"F1.opExtrude","CAP_FACE",FACE,{"disambiguationData":[OSD([sQuery(id+"F0.wireOp",EDGE,"E0"),subQ1,sQuery(id+"F0.wireOp",EDGE,"E3"),sQuery(id+"F0.wireOp",EDGE,"E4"),subQ0,sQuery(id+"F0.wireOp",EDGE,"E5.1.1"),sQuery(id+"F0.wireOp",EDGE,"E5.2.0"),sQuery(id+"F0.wireOp",EDGE,"E5.2.1")])],"isStart":true})],"blendedInto":[makeQuery(id+"F1.opExtrude","CAP_FACE",FACE,{"disambiguationData":[OSD([sQuery(id+"F0.wireOp",EDGE,"E0"),subQ1,sQuery(id+"F0.wireOp",EDGE,"E3"),sQuery(id+"F0.wireOp",EDGE,"E4"),subQ0,sQuery(id+"F0.wireOp",EDGE,"E5.1.1"),sQuery(id+"F0.wireOp",EDGE,"E5.2.0"),sQuery(id+"F0.wireOp",EDGE,"E5.2.1")])],"isStart":true})]});}
            var Q40;
            {var subQ0=sQuery(id+"F0.wireOp",EDGE,"E1");var subQ1=sQuery(id+"F0.wireOp",EDGE,"E5.1.0");var subQ2=makeQuery(id+"F0.imprint","INTERSECT",VERTEX,{"disambiguationData":[OD(1.0)],"derivedFrom":[subQ0,subQ1]});Q40=makeQuery(id+"F2.opFillet","BLEND_EDGE",EDGE,{"blendedFrom":[makeQuery(id+"F1.opExtrude","SWEPT_EDGE",EDGE,{"disambiguationData":[OSD([subQ0,subQ1]),TDD([subQ2])]}),makeQuery(id+"F1.opExtrude","SWEPT_FACE",FACE,{"disambiguationData":[OSD([subQ0]),TDD([makeQuery(id+"F0.imprint","IMPRINT",EDGE,{"disambiguationData":[TD([[makeQuery(id+"F0.imprint","INTERSECT",VERTEX,{"disambiguationData":[OD(1.0)],"derivedFrom":[subQ0,sQuery(id+"F0.wireOp",EDGE,"E3")]}),-1.0]])],"derivedFrom":subQ0})])]})],"blendedInto":[makeQuery(id+"F1.opExtrude","SWEPT_FACE",FACE,{"disambiguationData":[OSD([subQ0]),TDD([makeQuery(id+"F0.imprint","IMPRINT",EDGE,{"disambiguationData":[TD([[makeQuery(id+"F0.imprint","INTERSECT",VERTEX,{"disambiguationData":[OD(1.0)],"derivedFrom":[subQ0,sQuery(id+"F0.wireOp",EDGE,"E3")]}),-1.0]])],"derivedFrom":subQ0})])]})]});}
            var Q41;
            {var subQ0=sQuery(id+"F0.wireOp",EDGE,"E1");Q41=makeQuery(id+"F1.opExtrude","CAP_EDGE",EDGE,{"disambiguationData":[OSD([subQ0]),TDD([makeQuery(id+"F0.imprint","IMPRINT",EDGE,{"disambiguationData":[TD([[makeQuery(id+"F0.imprint","INTERSECT",VERTEX,{"disambiguationData":[OD(0.0)],"derivedFrom":[subQ0,sQuery(id+"F0.wireOp",EDGE,"E5.1.0")]}),-1.0]])],"derivedFrom":subQ0})])],"isStart":true});}
            var Q42;
            {var subQ0=sQuery(id+"F0.wireOp",EDGE,"E1");Q42=makeQuery(id+"F1.opExtrude","CAP_EDGE",EDGE,{"disambiguationData":[OSD([subQ0]),TDD([makeQuery(id+"F0.imprint","IMPRINT",EDGE,{"disambiguationData":[TD([[makeQuery(id+"F0.imprint","INTERSECT",VERTEX,{"disambiguationData":[OD(0.0)],"derivedFrom":[subQ0,sQuery(id+"F0.wireOp",EDGE,"E5.1.0")]}),-1.0]])],"derivedFrom":subQ0})])],"isStart":false});}
            var Q43;
            {var subQ0=sQuery(id+"F0.wireOp",EDGE,"E1");Q43=makeQuery(id+"F1.opExtrude","CAP_EDGE",EDGE,{"disambiguationData":[OSD([subQ0]),TDD([makeQuery(id+"F0.imprint","IMPRINT",EDGE,{"disambiguationData":[TD([[makeQuery(id+"F0.imprint","INTERSECT",VERTEX,{"disambiguationData":[OD(1.0)],"derivedFrom":[subQ0,sQuery(id+"F0.wireOp",EDGE,"E5.2.0")]}),-1.0]])],"derivedFrom":subQ0})])],"isStart":true});}
            fillet(context, id + "F3", {"entities" : qUnion([Q0, Q1, Q2, Q3, Q4, Q5, Q6, Q7, Q8, Q9, Q10, Q11, Q12, Q13, Q14, Q15, Q16, Q17, Q18, Q19, Q20, Q21, Q22, Q23, Q24, Q25, Q26, Q27, Q28, Q29, Q30, Q31, Q32, Q33, Q34, Q35, Q36, Q37, Q38, Q39, Q40, Q41, Q42, Q43]), "radius" : 1 * mm, "tangentPropagation" : true, "allowEdgeOverflow" : false});
        }
    });
